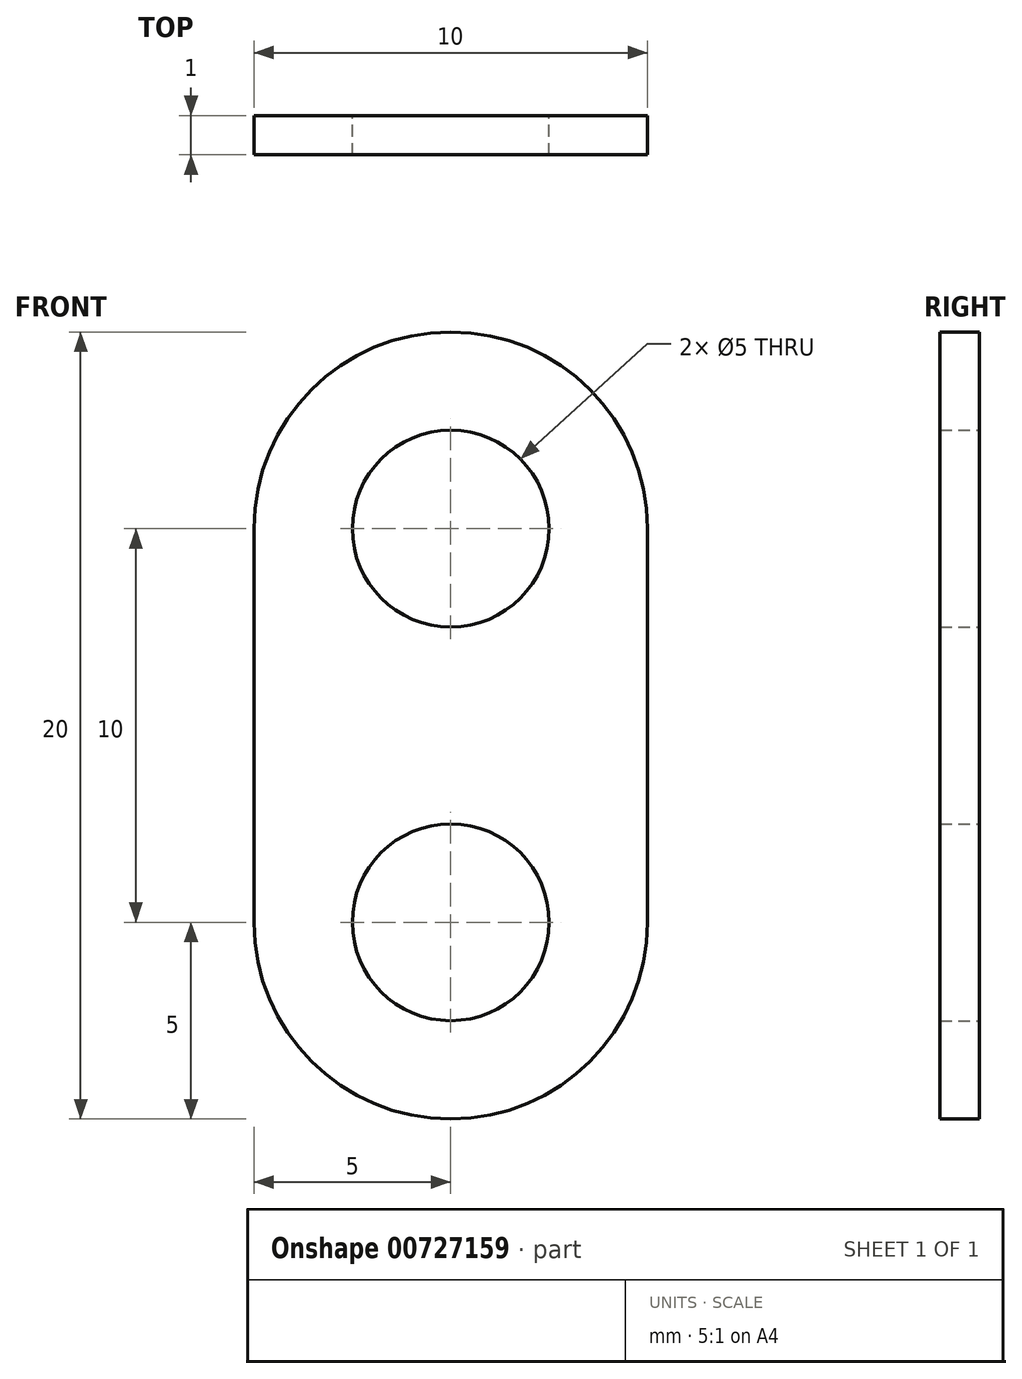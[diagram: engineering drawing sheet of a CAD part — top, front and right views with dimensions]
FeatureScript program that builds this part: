
annotation { "Feature Type Name" : "Feature", "Feature Type Description" : "" }
export const myFeature = defineFeature(function(context is Context, id is Id, definition is map)
    precondition{}
    {
        {
            var Q0;
            Q0=qCreatedBy(makeId("Front.planeOp"),FACE);
            var sketch = newSketch(context, id + "F0", { "sketchPlane" : qUnion([Q0])});
            skArc(sketch, "E0", {"start": v(5, 0) * mm, "mid": v(0, 5) * mm, "end": v(-5, 0) * mm});
            skArc(sketch, "E1", {"start": v(-5, -10) * mm, "mid": v(0, -15) * mm, "end": v(5, -10) * mm});
            skCircle(sketch, "E2", {"center": v(0, 0) * mm, "radius": 2.5 * mm});
            skCircle(sketch, "E3", {"center": v(0, -10) * mm, "radius": 2.5 * mm});
            skLineSegment(sketch, "E4", {"start": v(-5, -10) * mm, "end": v(-5, 0) * mm});
            skLineSegment(sketch, "E5", {"start": v(5, -10) * mm, "end": v(5, 0) * mm});
            skSolve(sketch);
        }
        {
            var Q0;
            Q0 = qSketchRegion(id + "F0", true);
            extrude(context, id + "F1", {"entities" : qUnion([Q0]), "depth" : 1 * mm, "offsetDistance" : 25.4 * mm});
        }
    });
